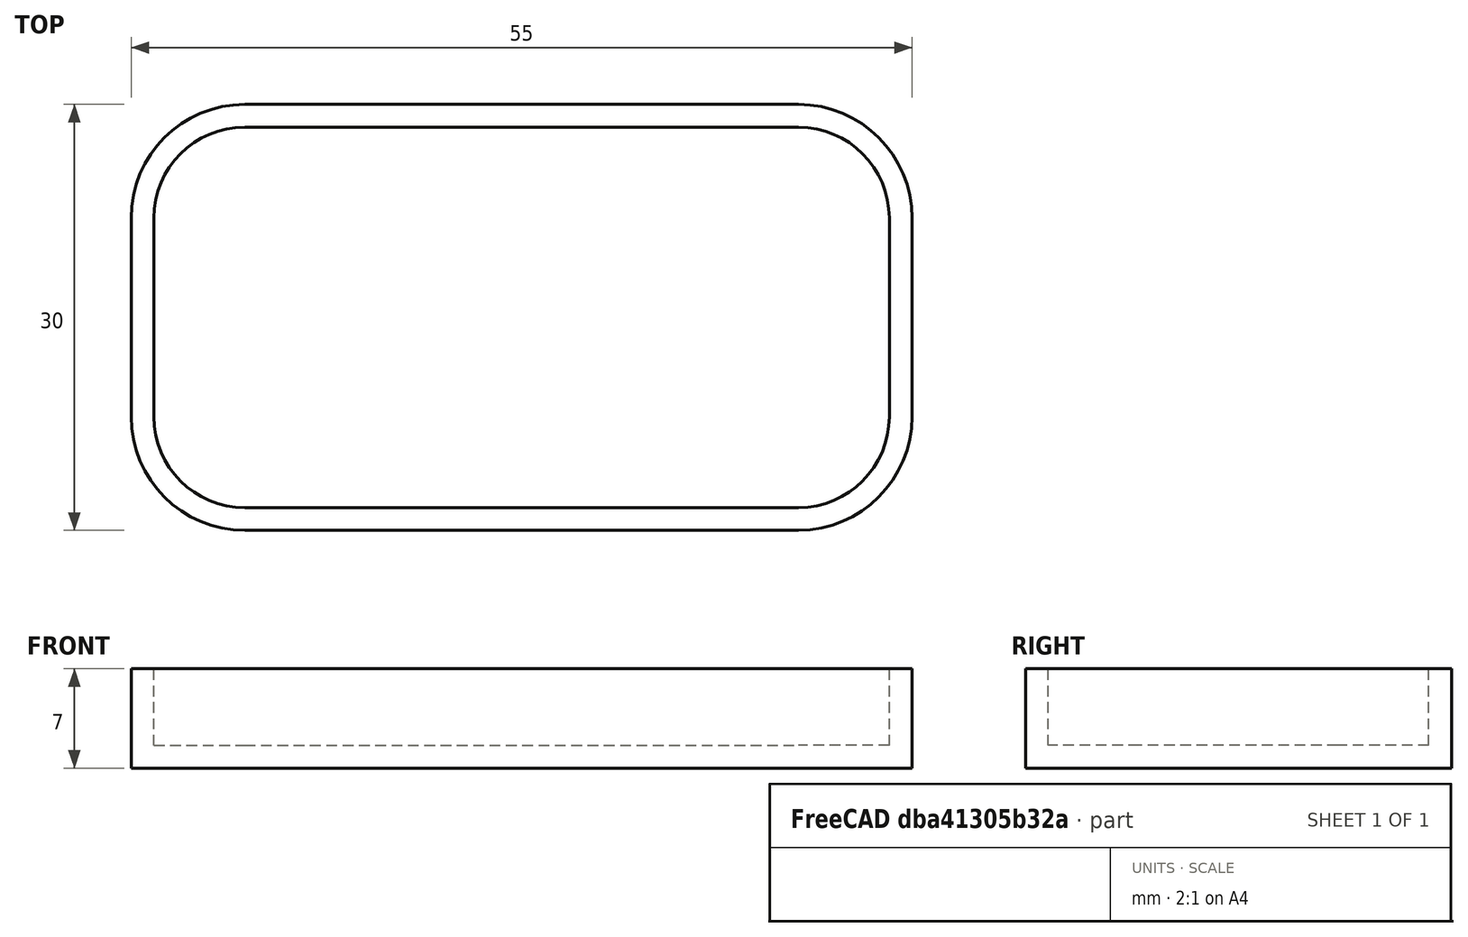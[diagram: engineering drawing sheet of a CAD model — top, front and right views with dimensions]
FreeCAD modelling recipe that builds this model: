
FCSTD DOCUMENT  (FreeCAD 1.0R39319 (Git))
Label: challenge1
License: All rights reserved
LicenseURL: https://en.wikipedia.org/wiki/All_rights_reserved
objects: PartDesign::Pad×2, Sketcher::SketchObject×1, PartDesign::Body×1
note: 9 computed .brp shape members not serialized (recipe doc carries the construction recipe); baked Part::Feature solids carry a one-line shape summary decoded from their .brp

FEATURE [Sketcher::SketchObject] Sketch
  ArcFitTolerance = 1e-06
  AttachmentSupport = -> [XY_Plane]
  FullyConstrained = false
  MakeInternals = false
  MapMode = 5
  sketch-geometry (20):
    g0: LineSegment StartX=-27.5 StartY=7 StartZ=0 EndX=-27.5 EndY=-7 EndZ=0
    g1: LineSegment StartX=-19.5 StartY=-15 StartZ=0 EndX=19.5 EndY=-15 EndZ=0
    g2: LineSegment StartX=27.5 StartY=-7 StartZ=0 EndX=27.5 EndY=7 EndZ=0
    g3: LineSegment StartX=19.5 StartY=15 StartZ=0 EndX=-19.5 EndY=15 EndZ=0
    g4: ArcOfCircle CenterX=-19.5 CenterY=-7 CenterZ=0 NormalX=0 NormalY=0 NormalZ=1 AngleXU=0 Radius=8 StartAngle=3.14159 EndAngle=4.71239
    g5: GeomPoint [constr] X=-27.5 Y=-15 Z=0
    g6: ArcOfCircle CenterX=-19.5 CenterY=7 CenterZ=0 NormalX=0 NormalY=0 NormalZ=1 AngleXU=0 Radius=8 StartAngle=1.5708 EndAngle=3.14159
    g7: GeomPoint [constr] X=-27.5 Y=15 Z=0
    g8: ArcOfCircle CenterX=19.5 CenterY=7 CenterZ=0 NormalX=0 NormalY=0 NormalZ=1 AngleXU=0 Radius=8 StartAngle=2.34e-14 EndAngle=1.5708
    g9: GeomPoint [constr] X=27.5 Y=15 Z=0
    g10: ArcOfCircle CenterX=19.5 CenterY=-7 CenterZ=0 NormalX=0 NormalY=0 NormalZ=1 AngleXU=0 Radius=8 StartAngle=4.71239 EndAngle=6.28319
    g11: GeomPoint [constr] X=27.5 Y=-15 Z=0
    g12: ArcOfCircle CenterX=19.5 CenterY=-7 CenterZ=0 NormalX=0 NormalY=0 NormalZ=1 AngleXU=0 Radius=6.4 StartAngle=4.71239 EndAngle=6.28319
    g13: LineSegment StartX=25.9 StartY=-7 StartZ=0 EndX=25.9 EndY=7 EndZ=0
    g14: ArcOfCircle CenterX=19.5 CenterY=7 CenterZ=0 NormalX=0 NormalY=0 NormalZ=1 AngleXU=0 Radius=6.4 StartAngle=0 EndAngle=1.5708
    g15: LineSegment StartX=19.5 StartY=13.4 StartZ=0 EndX=-19.5 EndY=13.4 EndZ=0
    g16: ArcOfCircle CenterX=-19.5 CenterY=7 CenterZ=0 NormalX=0 NormalY=0 NormalZ=1 AngleXU=0 Radius=6.4 StartAngle=1.5708 EndAngle=3.14159
    g17: LineSegment StartX=-25.9 StartY=7 StartZ=0 EndX=-25.9 EndY=-7 EndZ=0
    g18: ArcOfCircle CenterX=-19.5 CenterY=-7 CenterZ=0 NormalX=0 NormalY=0 NormalZ=1 AngleXU=0 Radius=6.4 StartAngle=3.14159 EndAngle=4.71239
    g19: LineSegment StartX=-19.5 StartY=-13.4 StartZ=0 EndX=19.5 EndY=-13.4 EndZ=0
  constraints (36):
    c: Vertical(g0)
    c: Vertical(g2)
    c: Horizontal(g1)
    c: Horizontal(g3)
    c: DistanceX(g5,g11) = 55
    c: DistanceY(g5,g7) = 30
    c: DistanceX(g-1,g9) = 27.5
    c: DistanceY(g11,g-1) = 15
    c: PointOnObject(g5,g0)
    c: PointOnObject(g5,g1)
    c: Tangent(g0,g4) = -1.5708
    c: Tangent(g1,g4) = -1.5708
    c: PointOnObject(g7,g0)
    c: PointOnObject(g7,g3)
    c: Tangent(g0,g6) = -1.5708
    c: Tangent(g3,g6) = -1.5708
    c: PointOnObject(g9,g2)
    c: PointOnObject(g9,g3)
    c: Tangent(g2,g8) = -1.5708
    c: Tangent(g3,g8) = -1.5708
    c: PointOnObject(g11,g1)
    c: PointOnObject(g11,g2)
    c: Tangent(g1,g10) = -1.5708
    c: Tangent(g2,g10) = -1.5708
    c: Equal(g6,g4)
    c: Equal(g10,g8)
    c: Equal(g8,g6)
    c: Radius(g6) = 8
    c: Tangent(g12,g13) = -1.5708
    c: Tangent(g12,g19) = -1.5708
    c: Tangent(g13,g14) = -1.5708
    c: Tangent(g14,g15) = -1.5708
    c: Tangent(g15,g16) = -1.5708
    c: Tangent(g16,g17) = -1.5708
    c: Tangent(g17,g18) = -1.5708
    c: Tangent(g18,g19) = -1.5708
FEATURE [PartDesign::Pad] Pad
  Direction = (0,0,1)
  Length = 1.6
  Length2 = 10
  Profile = -> Sketch [Edge5,Edge4,Edge3,Edge2,Edge1,Edge8,Edge7,Edge6]
  ReferenceAxis = -> Sketch [N_Axis]
  Refine = true
  Suppressed = false
  Type = 0
FEATURE [PartDesign::Pad] Pad001
  BaseFeature = -> Pad
  Direction = (0,0,1)
  Length = 7
  Length2 = 10
  Profile = -> Sketch
  ReferenceAxis = -> Sketch [N_Axis]
  Refine = true
  Suppressed = false
  Type = 0
FEATURE [PartDesign::Body] Body  label="tray"
  AllowCompound = false
  Group = -> [Sketch,Pad,Pad001]
  Origin = -> Origin
  Tip = -> Pad001
